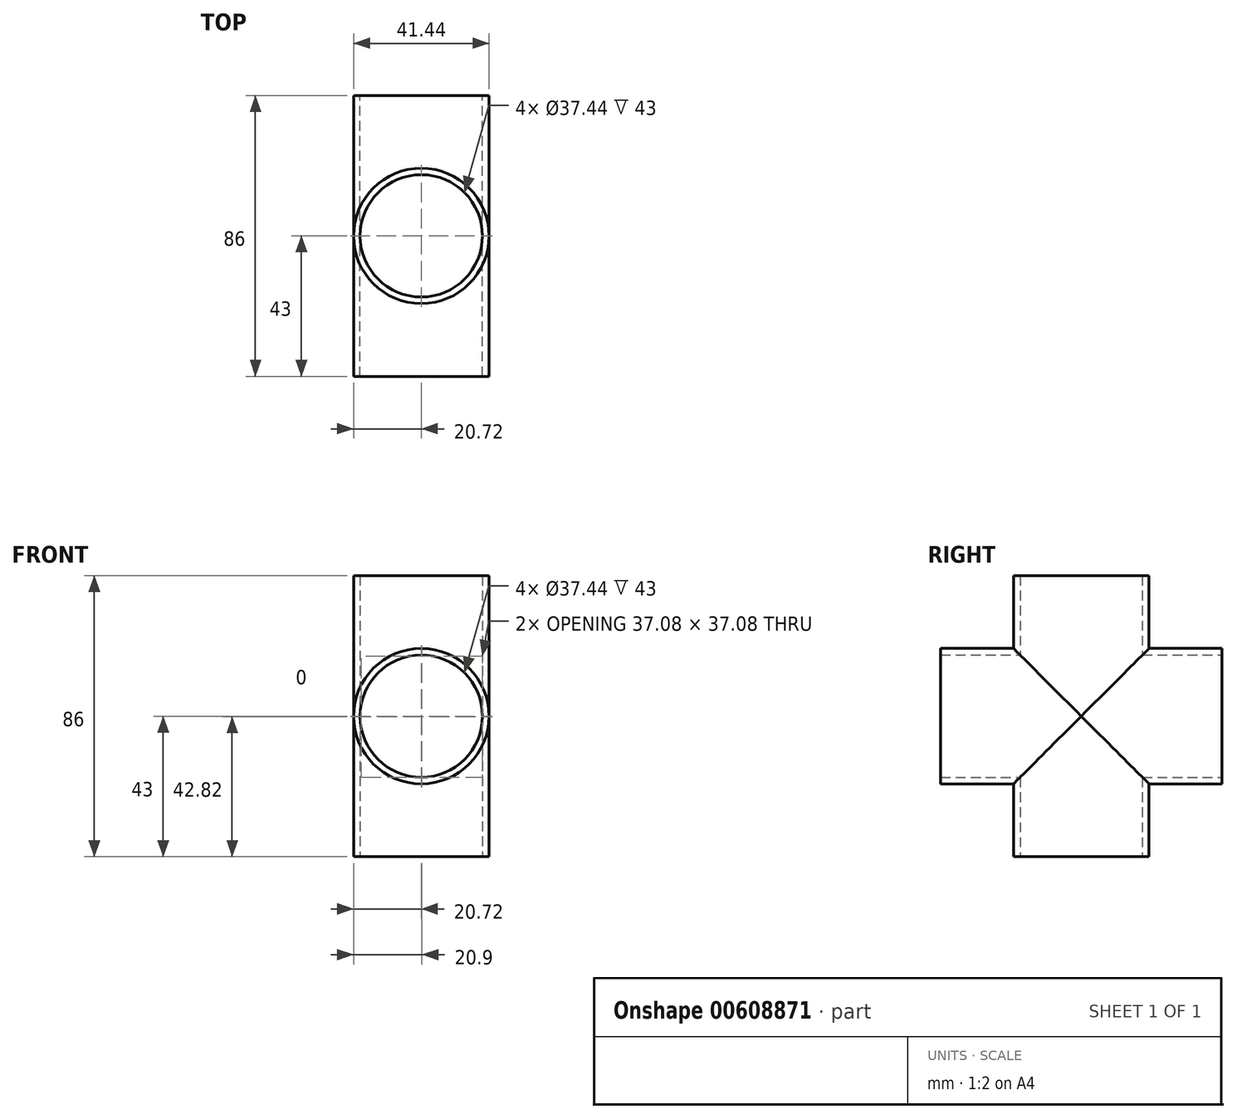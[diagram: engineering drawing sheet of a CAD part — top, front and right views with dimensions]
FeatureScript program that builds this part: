
annotation { "Feature Type Name" : "Feature", "Feature Type Description" : "" }
export const myFeature = defineFeature(function(context is Context, id is Id, definition is map)
    precondition{}
    {
        {
            var Q0;
            Q0=qCreatedBy(makeId("Top.planeOp"),FACE);
            var sketch = newSketch(context, id + "F0", { "sketchPlane" : qUnion([Q0])});
            skCircle(sketch, "E0", {"center": v(0, 0) * mm, "radius": 16.72 * mm});
            skSolve(sketch);
        }
        {
            var Q0;
            Q0=makeQuery(id+"F0.imprint","IMPRINT",FACE,{"disambiguationData":[TD([[makeQuery(id+"F0.imprint","IMPRINT",EDGE,{"derivedFrom":sQuery(id+"F0.wireOp",EDGE,"E0")}),1.0]])]});
            extrude(context, id + "F1", {"entities" : qUnion([Q0]), "endBound" : BoundingType.SYMMETRIC, "depth" : 86 * mm, "offsetDistance" : 25 * mm});
        }
        {
            var Q0;
            Q0=qCreatedBy(makeId("Front.planeOp"),FACE);
            var sketch = newSketch(context, id + "F2", { "sketchPlane" : qUnion([Q0])});
            skCircle(sketch, "E1", {"center": v(0, 0) * mm, "radius": 16.72 * mm});
            skSolve(sketch);
        }
        {
            var Q0;
            Q0 = qSketchRegion(id + "F2", true);
            extrude(context, id + "F3", {"entities" : qUnion([Q0]), "operationType" : NewBodyOperationType.ADD, "endBound" : BoundingType.SYMMETRIC, "depth" : 86 * mm, "offsetDistance" : 25 * mm});
        }
        {
            var Q0;
            Q0=makeQuery(id+"F1.opExtrude","CAP_FACE",FACE,{"disambiguationData":[OSD([sQuery(id+"F0.wireOp",EDGE,"E0")])],"isStart":true});
            var Q1;
            Q1=makeQuery(id+"F3.opExtrude","CAP_FACE",FACE,{"disambiguationData":[OSD([sQuery(id+"F2.wireOp",EDGE,"E1")])],"isStart":false});
            var Q2;
            Q2=makeQuery(id+"F1.opExtrude","CAP_FACE",FACE,{"disambiguationData":[OSD([sQuery(id+"F0.wireOp",EDGE,"E0")])],"isStart":false});
            var Q3;
            Q3=makeQuery(id+"F3.opExtrude","CAP_FACE",FACE,{"disambiguationData":[OSD([sQuery(id+"F2.wireOp",EDGE,"E1")])],"isStart":true});
            shell(context, id + "F4", {"entities" : qUnion([Q0, Q1, Q2, Q3]), "thickness" : 2 * mm, "oppositeDirection" : true});
        }
    });
